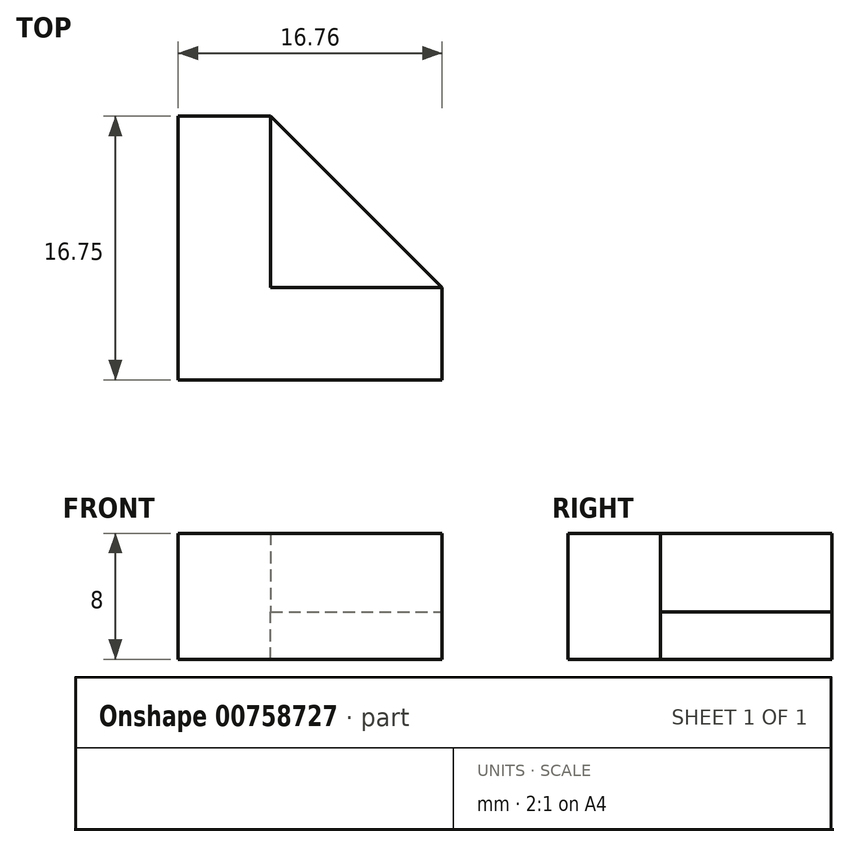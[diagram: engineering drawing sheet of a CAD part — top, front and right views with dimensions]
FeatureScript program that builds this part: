
annotation { "Feature Type Name" : "Feature", "Feature Type Description" : "" }
export const myFeature = defineFeature(function(context is Context, id is Id, definition is map)
    precondition{}
    {
        {
            var Q0;
            Q0=qCreatedBy(makeId("Top.planeOp"),FACE);
            var sketch = newSketch(context, id + "F0", { "sketchPlane" : qUnion([Q0])});
            skLineSegment(sketch, "E0", {"start": v(-62.95, -63.94) * mm, "end": v(-62.95, -47.19) * mm});
            skLineSegment(sketch, "E1", {"start": v(-62.95, -47.19) * mm, "end": v(-57.08, -47.19) * mm});
            skLineSegment(sketch, "E2", {"start": v(-57.08, -47.19) * mm, "end": v(-57.08, -58.07) * mm});
            skLineSegment(sketch, "E3", {"start": v(-57.08, -58.07) * mm, "end": v(-46.2, -58.07) * mm});
            skLineSegment(sketch, "E4", {"start": v(-46.2, -58.07) * mm, "end": v(-46.2, -63.94) * mm});
            skLineSegment(sketch, "E5", {"start": v(-46.2, -63.94) * mm, "end": v(-62.95, -63.94) * mm});
            skSolve(sketch);
        }
        {
            var Q0;
            Q0 = qSketchRegion(id + "F0", true);
            extrude(context, id + "F1", {"entities" : qUnion([Q0]), "endBound" : BoundingType.SYMMETRIC, "depth" : 5 * mm, "offsetDistance" : 25.4 * mm});
        }
        {
            var Q0;
            Q0=makeQuery(id+"F1.opExtrude","CAP_FACE",FACE,{"disambiguationData":[OSD([sQuery(id+"F0.wireOp",EDGE,"E0"),sQuery(id+"F0.wireOp",EDGE,"E1"),sQuery(id+"F0.wireOp",EDGE,"E2"),sQuery(id+"F0.wireOp",EDGE,"E3"),sQuery(id+"F0.wireOp",EDGE,"E4"),sQuery(id+"F0.wireOp",EDGE,"E5")])],"isStart":true});
            var sketch = newSketch(context, id + "F2", { "sketchPlane" : qUnion([Q0])});
            skLineSegment(sketch, "E6", {"start": v(-46.2, 63.94) * mm, "end": v(-46.2, 58.07) * mm});
            skLineSegment(sketch, "E7", {"start": v(-46.2, 58.07) * mm, "end": v(-57.08, 47.19) * mm});
            skLineSegment(sketch, "E8", {"start": v(-57.08, 47.19) * mm, "end": v(-62.95, 47.19) * mm});
            skLineSegment(sketch, "E9", {"start": v(-62.95, 47.19) * mm, "end": v(-62.95, 63.94) * mm});
            skLineSegment(sketch, "E10", {"start": v(-62.95, 63.94) * mm, "end": v(-46.2, 63.94) * mm});
            skSolve(sketch);
        }
        {
            var Q0;
            Q0 = qSketchRegion(id + "F2", true);
            extrude(context, id + "F3", {"entities" : qUnion([Q0]), "operationType" : NewBodyOperationType.ADD, "depth" : 3 * mm, "offsetDistance" : 25.4 * mm});
        }
    });
